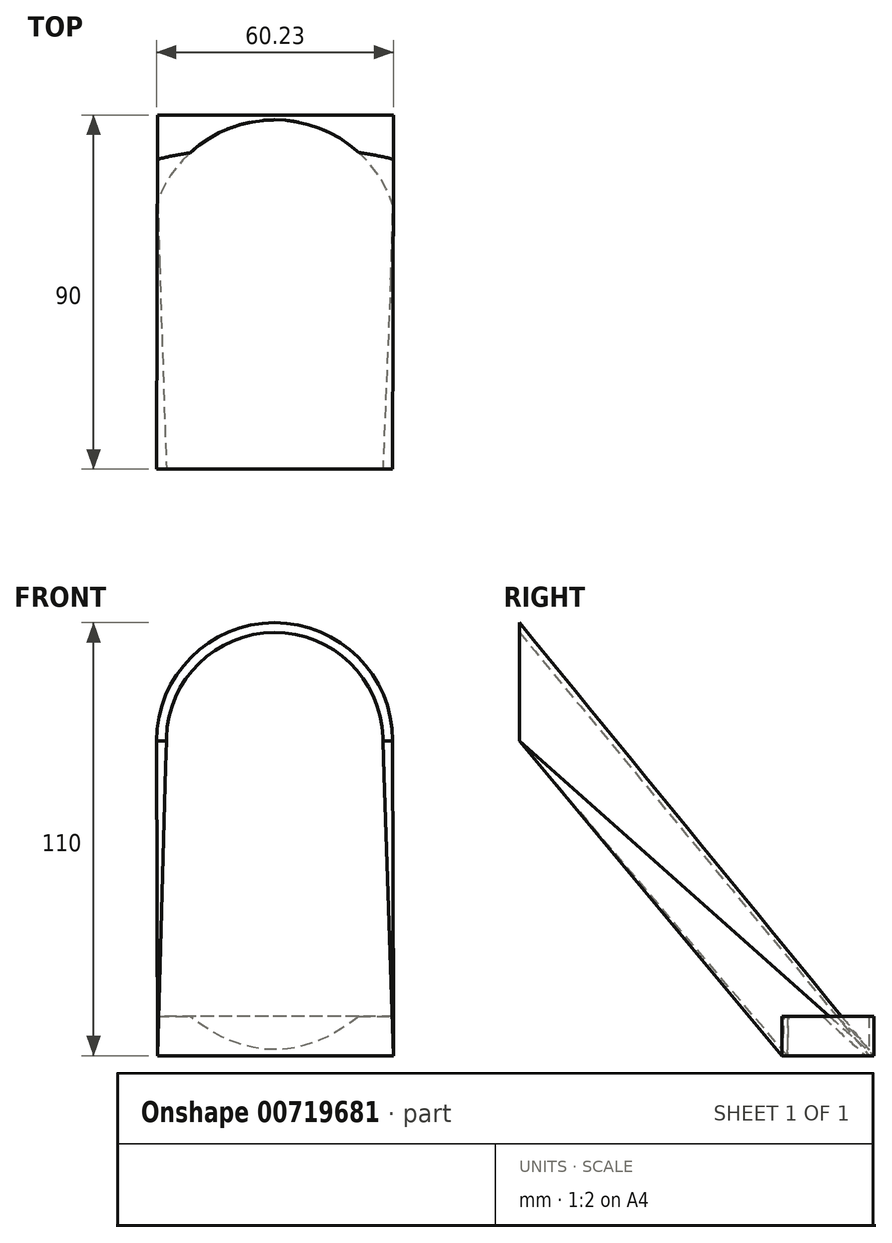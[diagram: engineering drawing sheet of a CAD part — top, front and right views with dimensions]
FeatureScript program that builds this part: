
annotation { "Feature Type Name" : "Feature", "Feature Type Description" : "" }
export const myFeature = defineFeature(function(context is Context, id is Id, definition is map)
    precondition{}
    {
        {
            var Q0;
            Q0=qCreatedBy(makeId("Front.planeOp"),FACE);
            var sketch = newSketch(context, id + "F0", { "sketchPlane" : qUnion([Q0])});
            skArc(sketch, "E0", {"start": v(30, 0) * mm, "mid": v(0, 30) * mm, "end": v(-30, 0) * mm});
            skLineSegment(sketch, "E1", {"start": v(30, 0) * mm, "end": v(27.5, 0) * mm});
            skArc(sketch, "E2", {"start": v(27.5, 0) * mm, "mid": v(0, 27.5) * mm, "end": v(-27.5, 0) * mm});
            skLineSegment(sketch, "E3.trimOffspring", {"start": v(-27.5, 0) * mm, "end": v(-30, 0) * mm});
            skSolve(sketch);
        }
        {
            var Q0;
            Q0=qCreatedBy(makeId("Top.planeOp"),FACE);
            cPlane(context, id + "F1", {"entities" : qUnion([Q0]), "cplaneType" : CPlaneType.OFFSET, "offset" : 80 * mm, "oppositeDirection" : true, "width" : 150 * mm, "height" : 150 * mm});
        }
        {
            var Q0;
            Q0=qCreatedBy(id+"F1.planeOp",FACE);
            var sketch = newSketch(context, id + "F2", { "sketchPlane" : qUnion([Q0])});
            skLineSegment(sketch, "E4.top", {"start": v(30.23, 90) * mm, "end": v(-29.77, 90) * mm});
            skLineSegment(sketch, "E4.left", {"start": v(30.23, 66.64) * mm, "end": v(30.23, 90) * mm});
            skLineSegment(sketch, "E4.right", {"start": v(-29.77, 68) * mm, "end": v(-29.77, 90) * mm});
            skArc(sketch, "E5", {"start": v(30.23, 66.64) * mm, "mid": v(0.72, 88.75) * mm, "end": v(-29.77, 68) * mm});
            skSolve(sketch);
        }
        {
            var Q0;
            {var subQ0=sQuery(id+"F2.wireOp",EDGE,"E4.right");Q0=makeQuery(id+"F2.imprint","IMPRINT",FACE,{"disambiguationData":[TD([[makeQuery(id+"F2.imprint","IMPRINT",EDGE,{"derivedFrom":subQ0}),-1.0]])]});}
            var Q1;
            Q1=makeQuery(id+"F0.imprint","IMPRINT",FACE,{"disambiguationData":[TD([[makeQuery(id+"F0.imprint","IMPRINT",EDGE,{"derivedFrom":sQuery(id+"F0.wireOp",EDGE,"E0")}),1.0]])]});
            loft(context, id + "F3", {"sheetProfilesArray" : [{ "sheetProfileEntities" : qUnion([Q0]) }, { "sheetProfileEntities" : qUnion([Q1]) }]});
        }
        {
            var Q0;
            Q0=makeQuery(id+"F3.opLoft","CAP_FACE",FACE,{"disambiguationData":[OSD([makeQuery(id+"F2.imprint","IMPRINT",FACE,{"disambiguationData":[TD([[makeQuery(id+"F2.imprint","IMPRINT",EDGE,{"derivedFrom":sQuery(id+"F2.wireOp",EDGE,"E4.top")}),1.0]])]})])],"isStart":true});
            var Q1;
            Q1=makeQuery(id+"F3.opLoft","SWEPT_FACE",FACE,{"disambiguationData":[OSD([sQuery(id+"F0.wireOp",EDGE,"E0"),sQuery(id+"F0.wireOp",EDGE,"E1"),sQuery(id+"F0.wireOp",EDGE,"E3.trimOffspring"),sQuery(id+"F2.wireOp",EDGE,"E4.top"),sQuery(id+"F2.wireOp",EDGE,"E4.left"),sQuery(id+"F2.wireOp",EDGE,"E4.right")])]});
            extrude(context, id + "F4", {"entities" : qUnion([Q0]), "operationType" : NewBodyOperationType.ADD, "oppositeDirection" : true, "depth" : 10 * mm, "endBoundEntityFace" : qUnion([Q1]), "offsetDistance" : 25 * mm});
        }
    });
